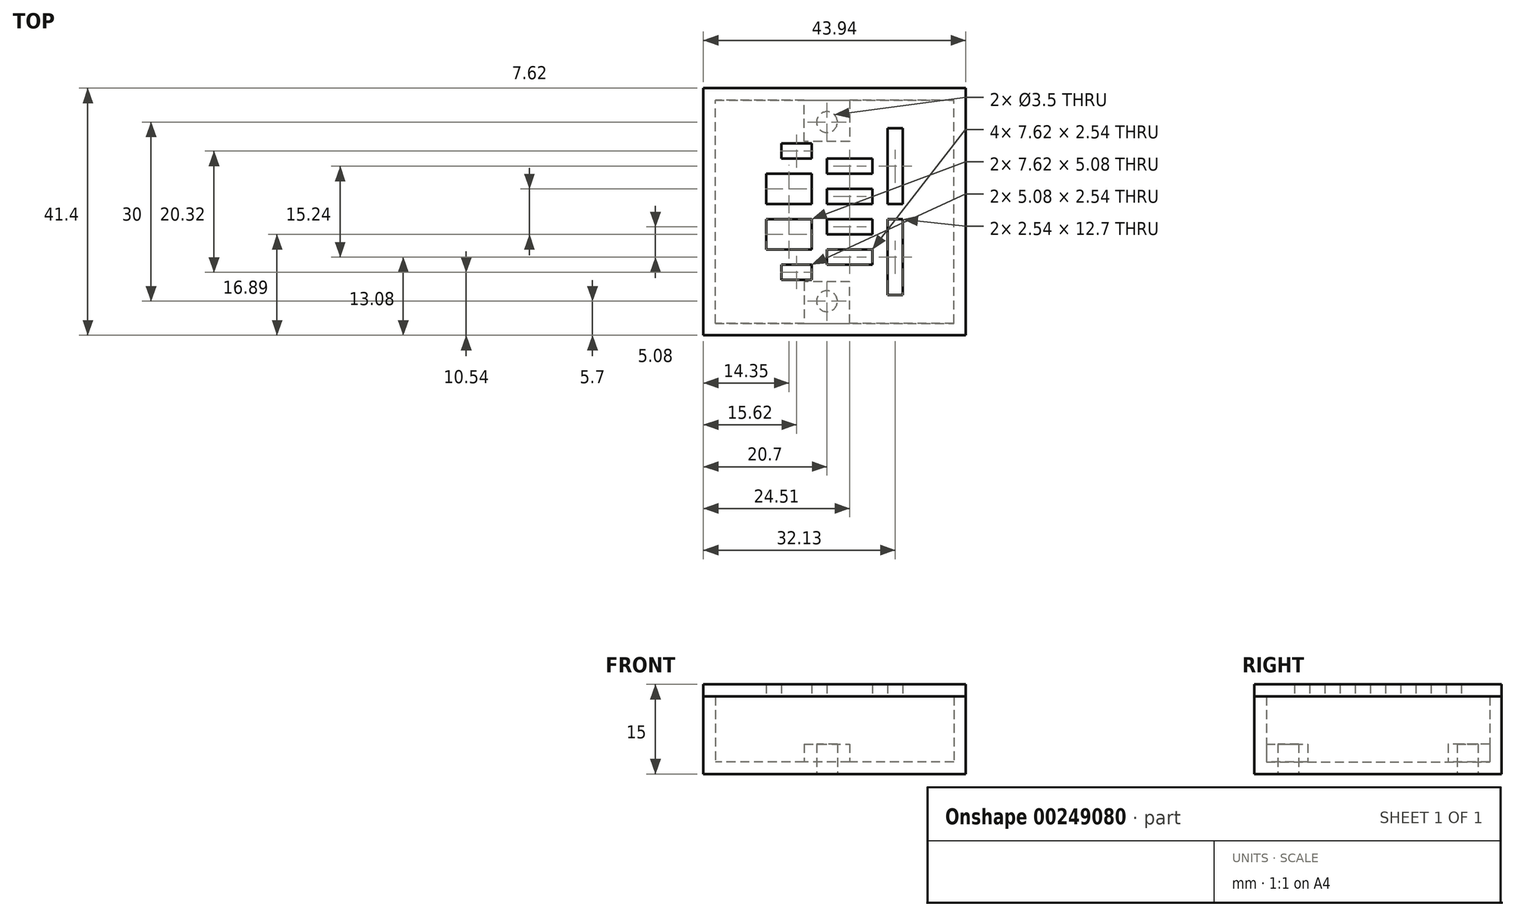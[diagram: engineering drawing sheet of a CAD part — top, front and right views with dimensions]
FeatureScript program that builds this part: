
annotation { "Feature Type Name" : "Feature", "Feature Type Description" : "" }
export const myFeature = defineFeature(function(context is Context, id is Id, definition is map)
    precondition{}
    {
        {
            var Q0;
            Q0=qCreatedBy(makeId("Top.planeOp"),FACE);
            var sketch = newSketch(context, id + "F0", { "sketchPlane" : qUnion([Q0])});
            skLineSegment(sketch, "E0.bottom", {"start": v(-13.97, 12.7) * mm, "end": v(13.97, 12.7) * mm, "construction": true});
            skLineSegment(sketch, "E0.top", {"start": v(-13.97, -12.7) * mm, "end": v(13.97, -12.7) * mm, "construction": true});
            skLineSegment(sketch, "E0.left", {"start": v(-13.97, 12.7) * mm, "end": v(-13.97, -12.7) * mm, "construction": true});
            skLineSegment(sketch, "E0.right", {"start": v(13.97, 12.7) * mm, "end": v(13.97, -12.7) * mm, "construction": true});
            skCircle(sketch, "E1", {"center": v(-13.97, 12.7) * mm, "radius": 1.25 * mm, "construction": true});
            skCircle(sketch, "E2", {"center": v(13.97, 12.7) * mm, "radius": 1.25 * mm, "construction": true});
            skCircle(sketch, "E3", {"center": v(13.97, -12.7) * mm, "radius": 1.25 * mm, "construction": true});
            skCircle(sketch, "E4", {"center": v(-13.97, -12.7) * mm, "radius": 1.25 * mm, "construction": true});
            skLineSegment(sketch, "E5.0", {"start": v(-19.97, 18.7) * mm, "end": v(-19.97, -18.7) * mm});
            skLineSegment(sketch, "E5.1", {"start": v(-19.97, 18.7) * mm, "end": v(19.97, 18.7) * mm});
            skLineSegment(sketch, "E5.2", {"start": v(19.97, 18.7) * mm, "end": v(19.97, -18.7) * mm});
            skLineSegment(sketch, "E5.3", {"start": v(-19.97, -18.7) * mm, "end": v(19.97, -18.7) * mm});
            skLineSegment(sketch, "E6.0", {"start": v(-21.97, 20.7) * mm, "end": v(-21.97, -20.7) * mm});
            skLineSegment(sketch, "E6.1", {"start": v(-21.97, 20.7) * mm, "end": v(21.97, 20.7) * mm});
            skLineSegment(sketch, "E6.2", {"start": v(21.97, 20.7) * mm, "end": v(21.97, -20.7) * mm});
            skLineSegment(sketch, "E6.3", {"start": v(-21.97, -20.7) * mm, "end": v(21.97, -20.7) * mm});
            skLineSegment(sketch, "E7", {"start": v(-1.27, -15) * mm, "end": v(-1.27, 15) * mm, "construction": true});
            skPoint(sketch, "E8", {"position": v(-1.27, 0) * mm});
            skCircle(sketch, "E9", {"center": v(-1.27, 15) * mm, "radius": 1.75 * mm});
            skCircle(sketch, "E10", {"center": v(-1.27, -15) * mm, "radius": 1.75 * mm});
            skLineSegment(sketch, "E11", {"start": v(-5.08, 18.7) * mm, "end": v(-5.08, 11.75) * mm});
            skLineSegment(sketch, "E12", {"start": v(-5.08, 11.75) * mm, "end": v(2.54, 11.75) * mm});
            skLineSegment(sketch, "E13", {"start": v(2.54, 11.75) * mm, "end": v(2.54, 18.7) * mm});
            skPoint(sketch, "E14", {"position": v(-1.27, 11.75) * mm});
            skLineSegment(sketch, "E15", {"start": v(-5.08, -18.7) * mm, "end": v(-5.08, -11.75) * mm});
            skLineSegment(sketch, "E16", {"start": v(-5.08, -11.75) * mm, "end": v(2.54, -11.75) * mm});
            skLineSegment(sketch, "E17", {"start": v(2.54, -11.75) * mm, "end": v(2.54, -18.7) * mm});
            skSolve(sketch);
        }
        {
            var Q0;
            Q0 = qSketchRegion(id + "F0", true);
            var Q1;
            Q1=makeQuery(id+"F0.imprint","IMPRINT",FACE,{"disambiguationData":[TD([[makeQuery(id+"F0.imprint","IMPRINT",EDGE,{"derivedFrom":sQuery(id+"F0.wireOp",EDGE,"E5.0")}),1.0]])]});
            var Q2;
            Q2=makeQuery(id+"F0.imprint","IMPRINT",FACE,{"disambiguationData":[TD([[makeQuery(id+"F0.imprint","IMPRINT",EDGE,{"derivedFrom":sQuery(id+"F0.wireOp",EDGE,"E4")}),-1.0]])]});
            var Q3;
            Q3=makeQuery(id+"F0.imprint","IMPRINT",FACE,{"disambiguationData":[TD([[makeQuery(id+"F0.imprint","IMPRINT",EDGE,{"derivedFrom":sQuery(id+"F0.wireOp",EDGE,"E1")}),-1.0]])]});
            var Q4;
            Q4=makeQuery(id+"F0.imprint","IMPRINT",FACE,{"disambiguationData":[TD([[makeQuery(id+"F0.imprint","IMPRINT",EDGE,{"derivedFrom":sQuery(id+"F0.wireOp",EDGE,"E2")}),-1.0]])]});
            var Q5;
            Q5=makeQuery(id+"F0.imprint","IMPRINT",FACE,{"disambiguationData":[TD([[makeQuery(id+"F0.imprint","IMPRINT",EDGE,{"derivedFrom":sQuery(id+"F0.wireOp",EDGE,"E3")}),-1.0]])]});
            var Q6;
            Q6=makeQuery(id+"F0.imprint","IMPRINT",FACE,{"disambiguationData":[TD([[makeQuery(id+"F0.imprint","IMPRINT",EDGE,{"derivedFrom":sQuery(id+"F0.wireOp",EDGE,"E9")}),-1.0]])]});
            var Q7;
            Q7=makeQuery(id+"F0.imprint","IMPRINT",FACE,{"disambiguationData":[TD([[makeQuery(id+"F0.imprint","IMPRINT",EDGE,{"derivedFrom":sQuery(id+"F0.wireOp",EDGE,"E10")}),-1.0]])]});
            extrude(context, id + "F1", {"entities" : qUnion([Q0, Q1, Q2, Q3, Q4, Q5, Q6, Q7]), "depth" : 2 * mm, "offsetDistance" : 25 * mm});
        }
        {
            var Q0;
            Q0=makeQuery(id+"F0.imprint","IMPRINT",FACE,{"disambiguationData":[TD([[makeQuery(id+"F0.imprint","IMPRINT",EDGE,{"derivedFrom":sQuery(id+"F0.wireOp",EDGE,"E5.0")}),-1.0]])]});
            var Q1;
            Q1=makeQuery(id+"F0.imprint","IMPRINT",FACE,{"disambiguationData":[TD([[makeQuery(id+"F0.imprint","IMPRINT",EDGE,{"derivedFrom":sQuery(id+"F0.wireOp",EDGE,"E3")}),-1.0]])]});
            var Q2;
            Q2=makeQuery(id+"F0.imprint","IMPRINT",FACE,{"disambiguationData":[TD([[makeQuery(id+"F0.imprint","IMPRINT",EDGE,{"derivedFrom":sQuery(id+"F0.wireOp",EDGE,"E4")}),-1.0]])]});
            var Q3;
            Q3=makeQuery(id+"F0.imprint","IMPRINT",FACE,{"disambiguationData":[TD([[makeQuery(id+"F0.imprint","IMPRINT",EDGE,{"derivedFrom":sQuery(id+"F0.wireOp",EDGE,"E1")}),-1.0]])]});
            var Q4;
            Q4=makeQuery(id+"F0.imprint","IMPRINT",FACE,{"disambiguationData":[TD([[makeQuery(id+"F0.imprint","IMPRINT",EDGE,{"derivedFrom":sQuery(id+"F0.wireOp",EDGE,"E2")}),-1.0]])]});
            extrude(context, id + "F2", {"entities" : qUnion([Q0, Q1, Q2, Q3, Q4]), "operationType" : NewBodyOperationType.ADD, "depth" : 13 * mm, "offsetDistance" : 25 * mm});
        }
        {
            var Q0;
            Q0=makeQuery(id+"F0.imprint","IMPRINT",FACE,{"disambiguationData":[TD([[makeQuery(id+"F0.imprint","IMPRINT",EDGE,{"derivedFrom":sQuery(id+"F0.wireOp",EDGE,"E9")}),-1.0]])]});
            var Q1;
            Q1=makeQuery(id+"F0.imprint","IMPRINT",FACE,{"disambiguationData":[TD([[makeQuery(id+"F0.imprint","IMPRINT",EDGE,{"derivedFrom":sQuery(id+"F0.wireOp",EDGE,"E10")}),-1.0]])]});
            extrude(context, id + "F3", {"entities" : qUnion([Q0, Q1]), "operationType" : NewBodyOperationType.ADD, "depth" : 5 * mm, "offsetDistance" : 25 * mm});
        }
        {
            var Q0;
            Q0=makeQuery(id+"F2.opExtrude","CAP_FACE",FACE,{"disambiguationData":[OSD([sQuery(id+"F0.wireOp",EDGE,"E5.0"),sQuery(id+"F0.wireOp",EDGE,"E5.1"),sQuery(id+"F0.wireOp",EDGE,"E5.2"),sQuery(id+"F0.wireOp",EDGE,"E5.3"),sQuery(id+"F0.wireOp",EDGE,"E6.0"),sQuery(id+"F0.wireOp",EDGE,"E6.1"),sQuery(id+"F0.wireOp",EDGE,"E6.2"),sQuery(id+"F0.wireOp",EDGE,"E6.3")])],"isStart":false});
            var sketch = newSketch(context, id + "F4", { "sketchPlane" : qUnion([Q0])});
            skLineSegment(sketch, "E18.0", {"start": v(-21.97, 20.7) * mm, "end": v(-21.97, -20.7) * mm});
            skLineSegment(sketch, "E18.1", {"start": v(-21.97, 20.7) * mm, "end": v(21.97, 20.7) * mm});
            skLineSegment(sketch, "E18.2", {"start": v(-21.97, -20.7) * mm, "end": v(21.97, -20.7) * mm});
            skLineSegment(sketch, "E18.3", {"start": v(21.97, 20.7) * mm, "end": v(21.97, -20.7) * mm});
            skLineSegment(sketch, "E19", {"start": v(-21.97, 0) * mm, "end": v(21.97, 0) * mm, "construction": true});
            skLineSegment(sketch, "E20.bottom", {"start": v(8.9, 13.97) * mm, "end": v(11.43, 13.97) * mm});
            skLineSegment(sketch, "E20.top", {"start": v(8.9, 1.27) * mm, "end": v(11.43, 1.27) * mm});
            skLineSegment(sketch, "E20.left", {"start": v(8.9, 13.97) * mm, "end": v(8.9, 11.43) * mm});
            skLineSegment(sketch, "E20.right", {"start": v(11.43, 13.97) * mm, "end": v(11.43, 1.27) * mm});
            skCircle(sketch, "E21.0", {"center": v(-13.97, 12.7) * mm, "radius": 1.25 * mm, "construction": true});
            skCircle(sketch, "E21.1", {"center": v(13.97, 12.7) * mm, "radius": 1.25 * mm, "construction": true});
            skCircle(sketch, "E21.2", {"center": v(13.97, -12.7) * mm, "radius": 1.25 * mm, "construction": true});
            skCircle(sketch, "E21.3", {"center": v(-13.97, -12.7) * mm, "radius": 1.25 * mm, "construction": true});
            skLineSegment(sketch, "E22.bottom", {"start": v(-1.27, 3.8) * mm, "end": v(6.35, 3.8) * mm});
            skLineSegment(sketch, "E22.top", {"start": v(-1.27, 1.27) * mm, "end": v(6.35, 1.27) * mm});
            skLineSegment(sketch, "E22.left", {"start": v(-1.27, 3.8) * mm, "end": v(-1.27, 1.27) * mm});
            skLineSegment(sketch, "E22.right", {"start": v(6.35, 3.8) * mm, "end": v(6.35, 1.27) * mm});
            skLineSegment(sketch, "E23.bottom", {"start": v(-11.43, 6.35) * mm, "end": v(-3.8, 6.35) * mm});
            skLineSegment(sketch, "E23.top", {"start": v(-11.43, 1.27) * mm, "end": v(-3.8, 1.27) * mm});
            skLineSegment(sketch, "E23.left", {"start": v(-11.43, 6.35) * mm, "end": v(-11.43, 1.27) * mm});
            skLineSegment(sketch, "E23.right", {"start": v(-3.8, 6.35) * mm, "end": v(-3.8, 1.27) * mm});
            skLineSegment(sketch, "E24", {"start": v(10.16, 13.97) * mm, "end": v(10.16, 1.27) * mm, "construction": true});
            skLineSegment(sketch, "E25", {"start": v(8.9, 12.7) * mm, "end": v(11.43, 12.7) * mm, "construction": true});
            skLineSegment(sketch, "E26", {"start": v(8.9, 11.43) * mm, "end": v(8.9, 1.27) * mm});
            skPoint(sketch, "E27", {"position": v(10.16, 12.7) * mm});
            skLineSegment(sketch, "E28.bottom", {"start": v(-1.27, 8.9) * mm, "end": v(6.35, 8.9) * mm});
            skLineSegment(sketch, "E28.top", {"start": v(-1.27, 6.35) * mm, "end": v(6.35, 6.35) * mm});
            skLineSegment(sketch, "E28.left", {"start": v(-1.27, 8.9) * mm, "end": v(-1.27, 6.35) * mm});
            skLineSegment(sketch, "E28.right", {"start": v(6.35, 8.9) * mm, "end": v(6.35, 6.35) * mm});
            skLineSegment(sketch, "E29.bottom", {"start": v(-8.89, 11.43) * mm, "end": v(-3.8, 11.43) * mm});
            skLineSegment(sketch, "E29.top", {"start": v(-8.89, 8.9) * mm, "end": v(-3.8, 8.9) * mm});
            skLineSegment(sketch, "E29.left", {"start": v(-8.89, 11.43) * mm, "end": v(-8.89, 8.9) * mm});
            skLineSegment(sketch, "E29.right", {"start": v(-3.8, 11.43) * mm, "end": v(-3.8, 8.9) * mm});
            skLineSegment(sketch, "E30.MirrorCS", {"start": v(-11.43, -1.27) * mm, "end": v(-3.8, -1.27) * mm});
            skLineSegment(sketch, "E31.MirrorCS", {"start": v(-3.8, -6.35) * mm, "end": v(-3.8, -1.27) * mm});
            skLineSegment(sketch, "E32.MirrorCS", {"start": v(-11.43, -6.35) * mm, "end": v(-3.8, -6.35) * mm});
            skLineSegment(sketch, "E33.MirrorCS", {"start": v(-11.43, -6.35) * mm, "end": v(-11.43, -1.27) * mm});
            skLineSegment(sketch, "E34.MirrorCS", {"start": v(-8.89, -8.9) * mm, "end": v(-3.8, -8.9) * mm});
            skLineSegment(sketch, "E35.MirrorCS", {"start": v(-3.8, -11.43) * mm, "end": v(-3.8, -8.9) * mm});
            skLineSegment(sketch, "E36.MirrorCS", {"start": v(-8.89, -11.43) * mm, "end": v(-3.8, -11.43) * mm});
            skLineSegment(sketch, "E37.MirrorCS", {"start": v(-8.89, -11.43) * mm, "end": v(-8.89, -8.9) * mm});
            skLineSegment(sketch, "E38.MirrorCS", {"start": v(-1.27, -8.9) * mm, "end": v(-1.27, -6.35) * mm});
            skLineSegment(sketch, "E39.MirrorCS", {"start": v(-1.27, -8.9) * mm, "end": v(6.35, -8.9) * mm});
            skLineSegment(sketch, "E40.MirrorCS", {"start": v(6.35, -8.9) * mm, "end": v(6.35, -6.35) * mm});
            skLineSegment(sketch, "E41.MirrorCS", {"start": v(-1.27, -6.35) * mm, "end": v(6.35, -6.35) * mm});
            skLineSegment(sketch, "E42.MirrorCS", {"start": v(-1.27, -3.8) * mm, "end": v(6.35, -3.8) * mm});
            skLineSegment(sketch, "E43.MirrorCS", {"start": v(-1.27, -3.8) * mm, "end": v(-1.27, -1.27) * mm});
            skLineSegment(sketch, "E44.MirrorCS", {"start": v(-1.27, -1.27) * mm, "end": v(6.35, -1.27) * mm});
            skLineSegment(sketch, "E45.MirrorCS", {"start": v(6.35, -3.8) * mm, "end": v(6.35, -1.27) * mm});
            skLineSegment(sketch, "E46.MirrorCS", {"start": v(11.43, -13.97) * mm, "end": v(11.43, -1.27) * mm});
            skLineSegment(sketch, "E47.MirrorCS", {"start": v(8.9, -1.27) * mm, "end": v(11.43, -1.27) * mm});
            skLineSegment(sketch, "E48.MirrorCS", {"start": v(8.9, -13.97) * mm, "end": v(11.43, -13.97) * mm});
            skLineSegment(sketch, "E49", {"start": v(8.9, -1.27) * mm, "end": v(8.9, -13.97) * mm});
            skSolve(sketch);
        }
        {
            var Q0;
            Q0 = qSketchRegion(id + "F4", true);
            extrude(context, id + "F5", {"entities" : qUnion([Q0]), "depth" : 2 * mm, "offsetDistance" : 25 * mm});
        }
    });
